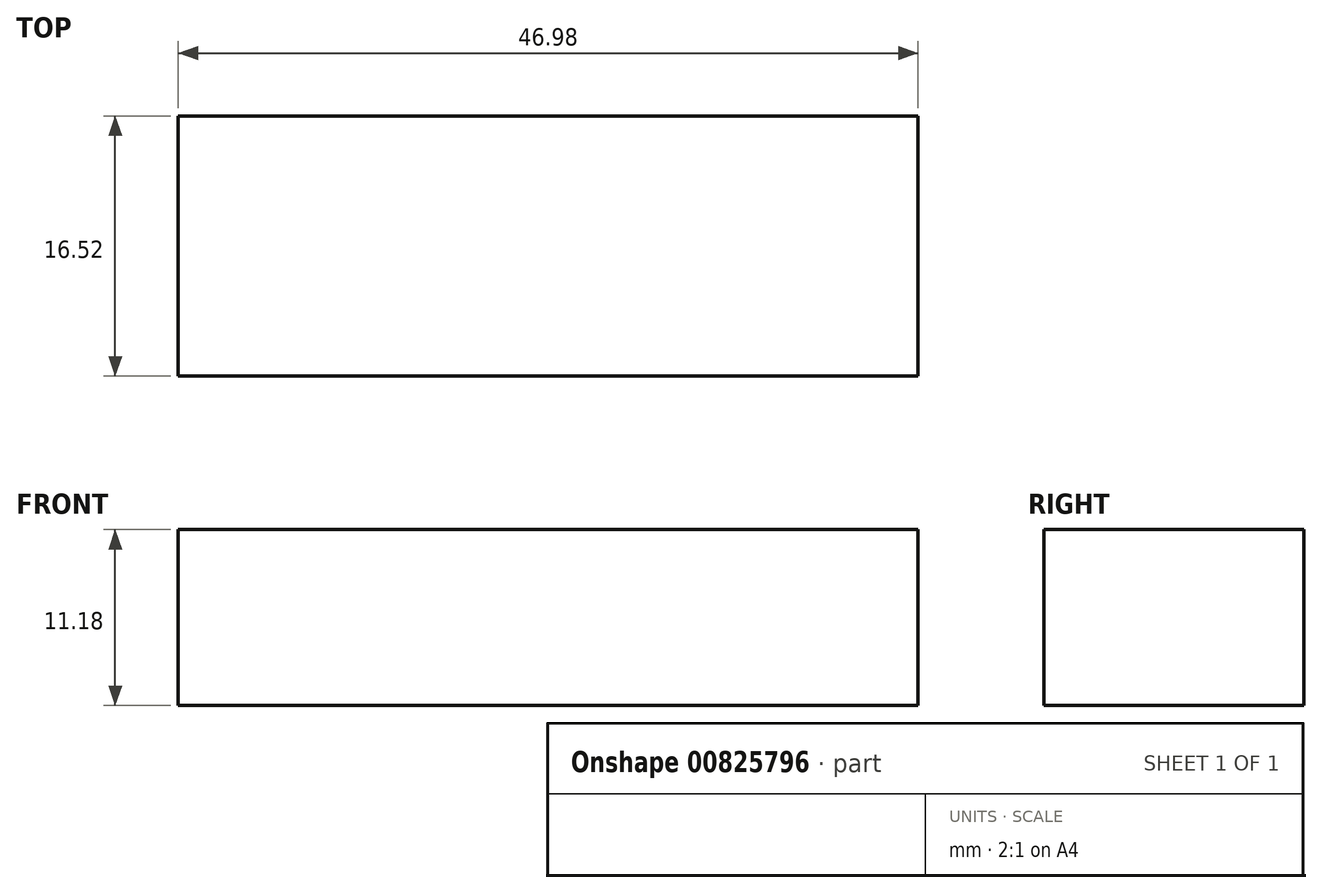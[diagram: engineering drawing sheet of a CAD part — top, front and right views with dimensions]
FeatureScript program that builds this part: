
annotation { "Feature Type Name" : "Feature", "Feature Type Description" : "" }
export const myFeature = defineFeature(function(context is Context, id is Id, definition is map)
    precondition{}
    {
        {
            var Q0;
            Q0=qCreatedBy(makeId("Top.planeOp"),FACE);
            var sketch = newSketch(context, id + "F0", { "sketchPlane" : qUnion([Q0])});
            skLineSegment(sketch, "E0.bottom", {"start": v(-23.5, 8.25) * mm, "end": v(23.5, 8.25) * mm});
            skLineSegment(sketch, "E0.top", {"start": v(-23.5, -8.26) * mm, "end": v(23.5, -8.26) * mm});
            skLineSegment(sketch, "E0.left", {"start": v(-23.5, 8.25) * mm, "end": v(-23.5, -8.26) * mm});
            skLineSegment(sketch, "E0.right", {"start": v(23.5, 8.25) * mm, "end": v(23.5, -8.26) * mm});
            skLineSegment(sketch, "E1", {"start": v(23.5, 8.26) * mm, "end": v(-23.5, -8.26) * mm, "construction": true});
            skPoint(sketch, "E2", {"position": v(0, 0) * mm});
            skSolve(sketch);
        }
        {
            var Q0;
            Q0 = qSketchRegion(id + "F0", true);
            extrude(context, id + "F1", {"entities" : qUnion([Q0]), "endBound" : BoundingType.SYMMETRIC, "depth" : 11.18 * mm, "offsetDistance" : 25.4 * mm});
        }
    });
